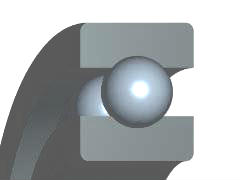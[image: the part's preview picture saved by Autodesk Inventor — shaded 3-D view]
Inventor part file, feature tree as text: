
AUTODESK INVENTOR PART (.ipt)
format: ipt  version: 2019 (Build 230136000, 136)  size: 460,800 bytes
history: native  units: mm (DEFAULTED — no unit token found)
features: other x3, plane x2, pattern_circular x1
ambient origin geometry x8: Origin, YZ Plane, XZ Plane, XY Plane, X Axis, Y Axis, Z Axis, Center Point
bodies: Solid1 (feature_tree)
feature tree (6):
  other  "WorkPoint1"
  other  "WorkAxis1"
  plane  "WorkPlane3"
  plane  "WorkPlane4"
  other  "WorkPoint2"
  pattern_circular  "Seriepolare1"  Count=2  [1 undecoded]
note: 1 required parameter value undecoded (feature->parameter linkage not recoverable at this tier; creation-order binding heuristic only, values carry confidence <= 0.55)
